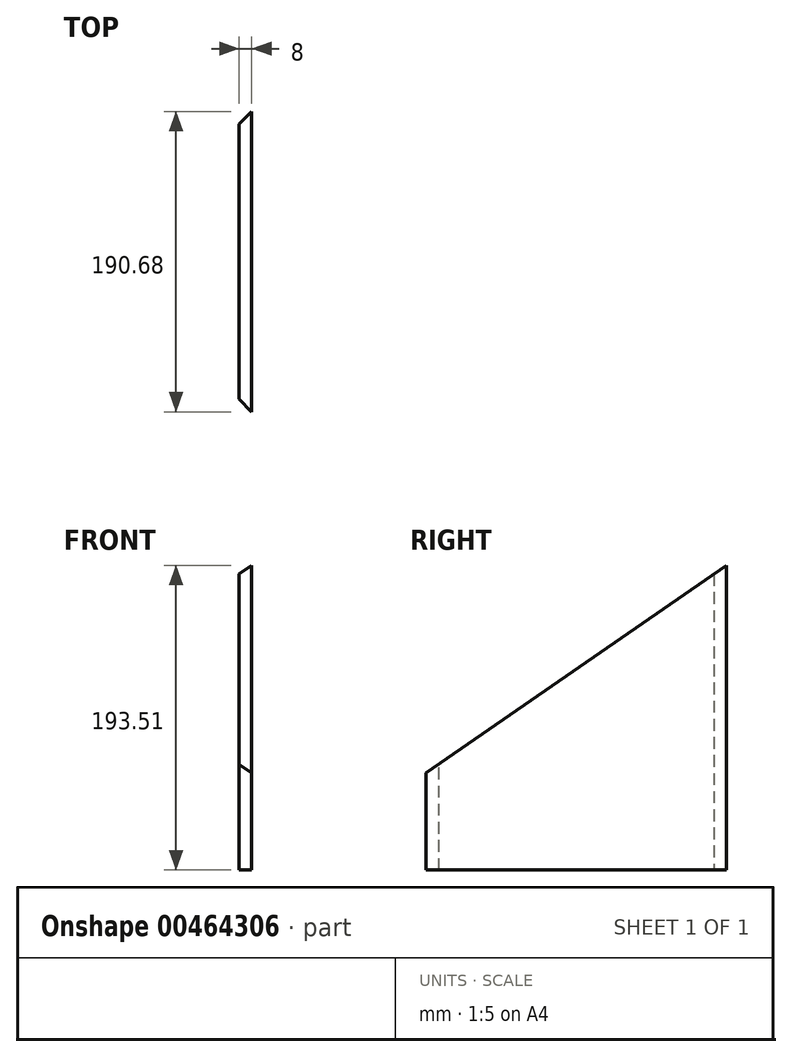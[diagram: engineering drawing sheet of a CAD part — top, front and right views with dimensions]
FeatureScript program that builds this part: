
annotation { "Feature Type Name" : "Feature", "Feature Type Description" : "" }
export const myFeature = defineFeature(function(context is Context, id is Id, definition is map)
    precondition{}
    {
        {
            var Q0;
            Q0=qCreatedBy(makeId("Right.planeOp"),FACE);
            var sketch = newSketch(context, id + "F0", { "sketchPlane" : qUnion([Q0])});
            skLineSegment(sketch, "E0.top", {"start": v(-99.98, -89.5) * mm, "end": v(95.02, -89.5) * mm});
            skPoint(sketch, "E0.middle", {"position": v(0, 0) * mm});
            skLineSegment(sketch, "E1", {"start": v(-99.98, -89.5) * mm, "end": v(-99.98, -29.5) * mm});
            skLineSegment(sketch, "E2", {"start": v(95.02, -89.5) * mm, "end": v(95.02, 105.5) * mm});
            skLineSegment(sketch, "E3", {"start": v(95.02, 105.5) * mm, "end": v(-99.98, -29.5) * mm});
            skSolve(sketch);
        }
        {
            var Q0;
            Q0=qSketchRegion(id+"F0",true);
            extrude(context, id + "F1", {"entities" : qUnion([Q0]), "endBound" : BoundingType.SYMMETRIC, "depth" : 8 * mm});
        }
        {
            var Q0;
            Q0=makeQuery(id+"F1.opExtrude","CAP_EDGE",EDGE,{"disambiguationData":[OSD([sQuery(id+"F0.wireOp",EDGE,"E1")])],"isStart":true});
            chamfer(context, id + "F2", {"entities" : qUnion([Q0]), "width" : 10.16 * mm, "tangentPropagation" : true});
        }
        {
            var Q0;
            Q0=makeQuery(id+"F1.opExtrude","CAP_EDGE",EDGE,{"disambiguationData":[OSD([sQuery(id+"F0.wireOp",EDGE,"E2")])],"isStart":true});
            chamfer(context, id + "F3", {"entities" : qUnion([Q0]), "width" : 10.16 * mm, "tangentPropagation" : true});
        }
    });
